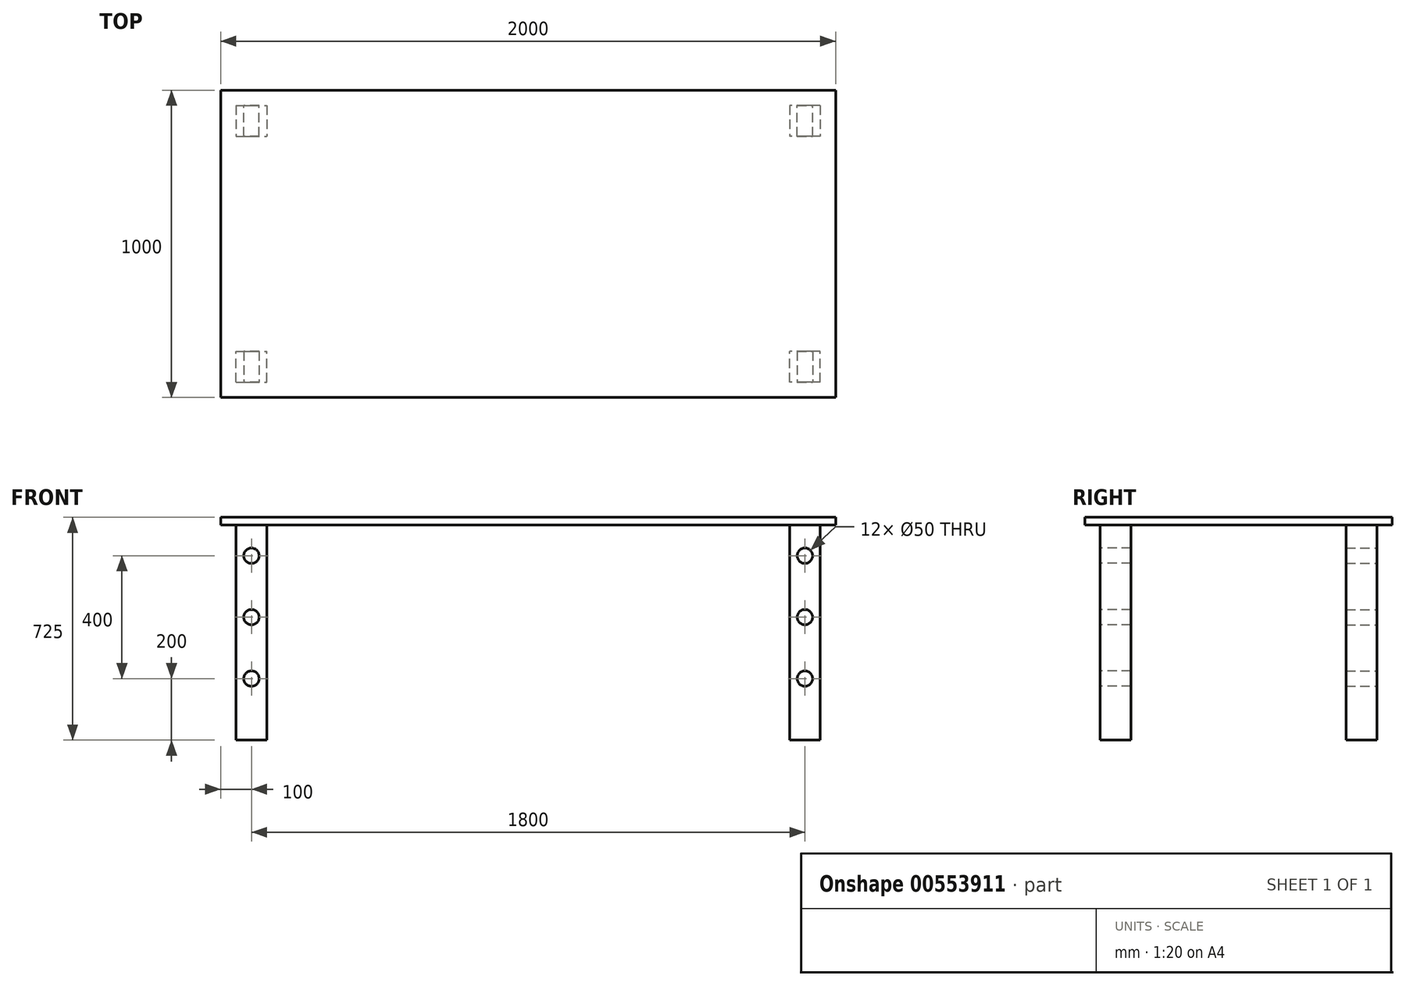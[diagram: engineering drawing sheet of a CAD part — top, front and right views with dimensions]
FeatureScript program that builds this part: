
annotation { "Feature Type Name" : "Feature", "Feature Type Description" : "" }
export const myFeature = defineFeature(function(context is Context, id is Id, definition is map)
    precondition{}
    {
        {
            var Q0;
            Q0=qCreatedBy(makeId("Top.planeOp"),FACE);
            var sketch = newSketch(context, id + "F0", { "sketchPlane" : qUnion([Q0])});
            skLineSegment(sketch, "E0.bottom", {"start": v(-496.22, 270.5) * mm, "end": v(503.78, 270.5) * mm});
            skLineSegment(sketch, "E0.top", {"start": v(-496.22, -229.5) * mm, "end": v(503.78, -229.5) * mm});
            skLineSegment(sketch, "E0.left", {"start": v(-496.22, 270.5) * mm, "end": v(-496.22, -229.5) * mm});
            skLineSegment(sketch, "E0.right", {"start": v(503.78, 270.5) * mm, "end": v(503.78, -229.5) * mm});
            skSolve(sketch);
        }
        {
            var Q0;
            Q0 = qSketchRegion(id + "F0", true);
            extrude(context, id + "F1", {"entities" : qUnion([Q0]), "depth" : 25 * mm, "offsetDistance" : 25 * mm});
        }
        {
            var Q0;
            Q0=makeQuery(id+"F1.opExtrude","CAP_FACE",FACE,{"disambiguationData":[OSD([sQuery(id+"F0.wireOp",EDGE,"E0.bottom"),sQuery(id+"F0.wireOp",EDGE,"E0.top"),sQuery(id+"F0.wireOp",EDGE,"E0.left"),sQuery(id+"F0.wireOp",EDGE,"E0.right")])],"isStart":true});
            var sketch = newSketch(context, id + "F2", { "sketchPlane" : qUnion([Q0])});
            skLineSegment(sketch, "E1.bottom", {"start": v(-446.22, 179.5) * mm, "end": v(-346.22, 179.5) * mm});
            skLineSegment(sketch, "E1.top", {"start": v(-446.22, 79.5) * mm, "end": v(-346.22, 79.5) * mm});
            skLineSegment(sketch, "E1.left", {"start": v(-446.22, 179.5) * mm, "end": v(-446.22, 79.5) * mm});
            skLineSegment(sketch, "E1.right", {"start": v(-346.22, 179.5) * mm, "end": v(-346.22, 79.5) * mm});
            skSolve(sketch);
        }
        {
            var Q0;
            Q0 = qSketchRegion(id + "F2", true);
            extrude(context, id + "F3", {"entities" : qUnion([Q0]), "operationType" : NewBodyOperationType.ADD, "depth" : 700 * mm, "offsetDistance" : 25 * mm});
        }
        {
            var Q0;
            Q0=makeQuery(id+"F3.opExtrude","SWEPT_FACE",FACE,{"disambiguationData":[OSD([sQuery(id+"F2.wireOp",EDGE,"E1.bottom")])]});
            var sketch = newSketch(context, id + "F4", { "sketchPlane" : qUnion([Q0])});
            skCircle(sketch, "E2", {"center": v(-396.22, -500) * mm, "radius": 20.12 * mm});
            skSolve(sketch);
        }
        {
            var Q0;
            Q0=sQuery(id+"F4.wireOp",VERTEX,"E2.center");
            var Q1;
            Q1=makeQuery(id+"F1.opExtrude","SWEPT_BODY",BODY,{"disambiguationData":[OSD([sQuery(id+"F0.wireOp",EDGE,"E0.bottom"),sQuery(id+"F0.wireOp",EDGE,"E0.top"),sQuery(id+"F0.wireOp",EDGE,"E0.left"),sQuery(id+"F0.wireOp",EDGE,"E0.right")])]});
            hole(context, id + "F5", {"style" : HoleStyle.SIMPLE, "endStyle" : HoleEndStyle.THROUGH, "holeDiameter" : 50 * mm, "isTappedThrough" : true, "tappedDepth" : 12 * mm, "tapClearance" : 3, "locations" : qUnion([Q0]), "scope" : qUnion([Q1])});
        }
        {
            var Q0;
            Q0=makeQuery(id+"F3.opExtrude","SWEPT_FACE",FACE,{"disambiguationData":[OSD([sQuery(id+"F2.wireOp",EDGE,"E1.bottom")])]});
            var sketch = newSketch(context, id + "F6", { "sketchPlane" : qUnion([Q0])});
            skCircle(sketch, "E3", {"center": v(-396.22, -300) * mm, "radius": 21.54 * mm});
            skSolve(sketch);
        }
        {
            var Q0;
            Q0=sQuery(id+"F6.wireOp",VERTEX,"E3.center");
            var Q1;
            Q1=makeQuery(id+"F1.opExtrude","SWEPT_BODY",BODY,{"disambiguationData":[OSD([sQuery(id+"F0.wireOp",EDGE,"E0.bottom"),sQuery(id+"F0.wireOp",EDGE,"E0.top"),sQuery(id+"F0.wireOp",EDGE,"E0.left"),sQuery(id+"F0.wireOp",EDGE,"E0.right")])]});
            hole(context, id + "F7", {"style" : HoleStyle.SIMPLE, "endStyle" : HoleEndStyle.THROUGH, "holeDiameter" : 50 * mm, "isTappedThrough" : true, "tappedDepth" : 12 * mm, "tapClearance" : 3, "locations" : qUnion([Q0]), "scope" : qUnion([Q1])});
        }
        {
            var Q0;
            Q0=makeQuery(id+"F3.opExtrude","SWEPT_FACE",FACE,{"disambiguationData":[OSD([sQuery(id+"F2.wireOp",EDGE,"E1.bottom")])]});
            var sketch = newSketch(context, id + "F8", { "sketchPlane" : qUnion([Q0])});
            skCircle(sketch, "E4", {"center": v(-396.22, -100) * mm, "radius": 21.32 * mm});
            skSolve(sketch);
        }
        {
            var Q0;
            Q0=sQuery(id+"F8.wireOp",VERTEX,"E4.center");
            var Q1;
            Q1=makeQuery(id+"F1.opExtrude","SWEPT_BODY",BODY,{"disambiguationData":[OSD([sQuery(id+"F0.wireOp",EDGE,"E0.bottom"),sQuery(id+"F0.wireOp",EDGE,"E0.top"),sQuery(id+"F0.wireOp",EDGE,"E0.left"),sQuery(id+"F0.wireOp",EDGE,"E0.right")])]});
            hole(context, id + "F9", {"style" : HoleStyle.SIMPLE, "endStyle" : HoleEndStyle.THROUGH, "holeDiameter" : 50 * mm, "isTappedThrough" : true, "tappedDepth" : 12 * mm, "tapClearance" : 3, "locations" : qUnion([Q0]), "scope" : qUnion([Q1])});
        }
        {
            var Q0;
            Q0=makeQuery(id+"F1.opExtrude","SWEPT_EDGE",EDGE,{"disambiguationData":[OSD([sQuery(id+"F0.wireOp",EDGE,"E0.bottom"),sQuery(id+"F0.wireOp",EDGE,"E0.right")])]});
            cPoint(context, id + "F10", {"entities" : qUnion([Q0]), "parameter" : 0.5});
        }
        {
            var Q0;
            Q0 = qCreatedBy(id + "F10" ,VERTEX);
            var Q1;
            Q1=makeQuery(id+"F1.opExtrude","SWEPT_FACE",FACE,{"disambiguationData":[OSD([sQuery(id+"F0.wireOp",EDGE,"E0.bottom")])]});
            cPlane(context, id + "F11", {"entities" : qUnion([Q0, Q1]), "cplaneType" : CPlaneType.PLANE_POINT, "offset" : 0 * mm, "width" : 150 * mm, "height" : 150 * mm});
        }
        {
            var Q0;
            Q0=makeQuery(id+"F1.opExtrude","SWEPT_BODY",BODY,{"disambiguationData":[OSD([sQuery(id+"F0.wireOp",EDGE,"E0.bottom"),sQuery(id+"F0.wireOp",EDGE,"E0.top"),sQuery(id+"F0.wireOp",EDGE,"E0.left"),sQuery(id+"F0.wireOp",EDGE,"E0.right")])]});
            var Q1;
            Q1=qCreatedBy(id+"F11.planeOp",FACE);
            mirror(context, id + "F12", {"operationType" : NewBodyOperationType.ADD, "entities" : qUnion([Q0]), "mirrorPlane" : qUnion([Q1])});
        }
        {
            var Q0;
            {var subQ0=makeQuery(id+"F1.opExtrude","SWEPT_FACE",FACE,{"disambiguationData":[OSD([sQuery(id+"F0.wireOp",EDGE,"E0.right")])]});Q0=makeQuery(id+"F12.boolean.opBoolean","MERGE",FACE,{"derivedFrom":[subQ0,makeQuery(id+"F12.opPattern","COPY",FACE,{"derivedFrom":subQ0,"instanceName":"1"})]});}
            cPlane(context, id + "F13", {"entities" : qUnion([Q0]), "cplaneType" : CPlaneType.OFFSET, "offset" : 0 * mm, "width" : 150 * mm, "height" : 150 * mm});
        }
        {
            var Q0;
            Q0=makeQuery(id+"F1.opExtrude","SWEPT_BODY",BODY,{"disambiguationData":[OSD([sQuery(id+"F0.wireOp",EDGE,"E0.bottom"),sQuery(id+"F0.wireOp",EDGE,"E0.top"),sQuery(id+"F0.wireOp",EDGE,"E0.left"),sQuery(id+"F0.wireOp",EDGE,"E0.right")])]});
            var Q1;
            Q1=qCreatedBy(id+"F13.planeOp",FACE);
            mirror(context, id + "F14", {"operationType" : NewBodyOperationType.ADD, "entities" : qUnion([Q0]), "mirrorPlane" : qUnion([Q1])});
        }
    });
